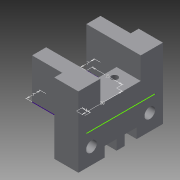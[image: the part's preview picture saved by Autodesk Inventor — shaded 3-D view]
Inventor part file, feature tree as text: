
AUTODESK INVENTOR PART (.ipt)
format: ipt  version: 2015 (Build 190159000, 159)  size: 148,992 bytes
history: native  units: in
note: dims shown in document units (in); Inventor stores cm internally (conversion verified against a paired STEP export)
features: extrude x7, sketch x4
ambient origin geometry x8: Origin, YZ Plane, XZ Plane, XY Plane, X Axis, Y Axis, Z Axis, Center Point
bodies: Solid1 (feature_tree)
feature tree (11):
  sketch  "Sketch1"  dims[d0=0.7874in d1=0.5906in]
  extrude  "Extrusion1"  Depth=0.5906in
  extrude  "Extrusion2"  Depth=0.2756in
  extrude  "Extrusion3"  Depth=0.7874in TaperAngle=0.0deg
  extrude  "Extrusion4"  Depth=0.5906in TaperAngle=0.0deg
  extrude  "Extrusion5"  Depth=0.3937in TaperAngle=0.0deg
  extrude  "Extrusion6"  Depth=0.1575in TaperAngle=0.0deg
  extrude  "Extrusion7"  Depth=0.1575in TaperAngle=0.0deg
  sketch  "Sketch2"  dims[d2=0.2756in d4=0.2756in]
  sketch  "Sketch3"  dims[d5=0.1575in d11=0.7874in d12=0.0in]
  sketch  "Sketch4"  dims[d13=0.3543in d14=0.0in d19=0.5906in d20=0.0in d21=0.3937in d22=0.0in d23=0.1575in d24=0.0in d25=0.1575in d26=0.0in d27=0.315in d28=0.315in d29=0.2087in d30=0.2087in d31=0.5118in d32=0.0in]
